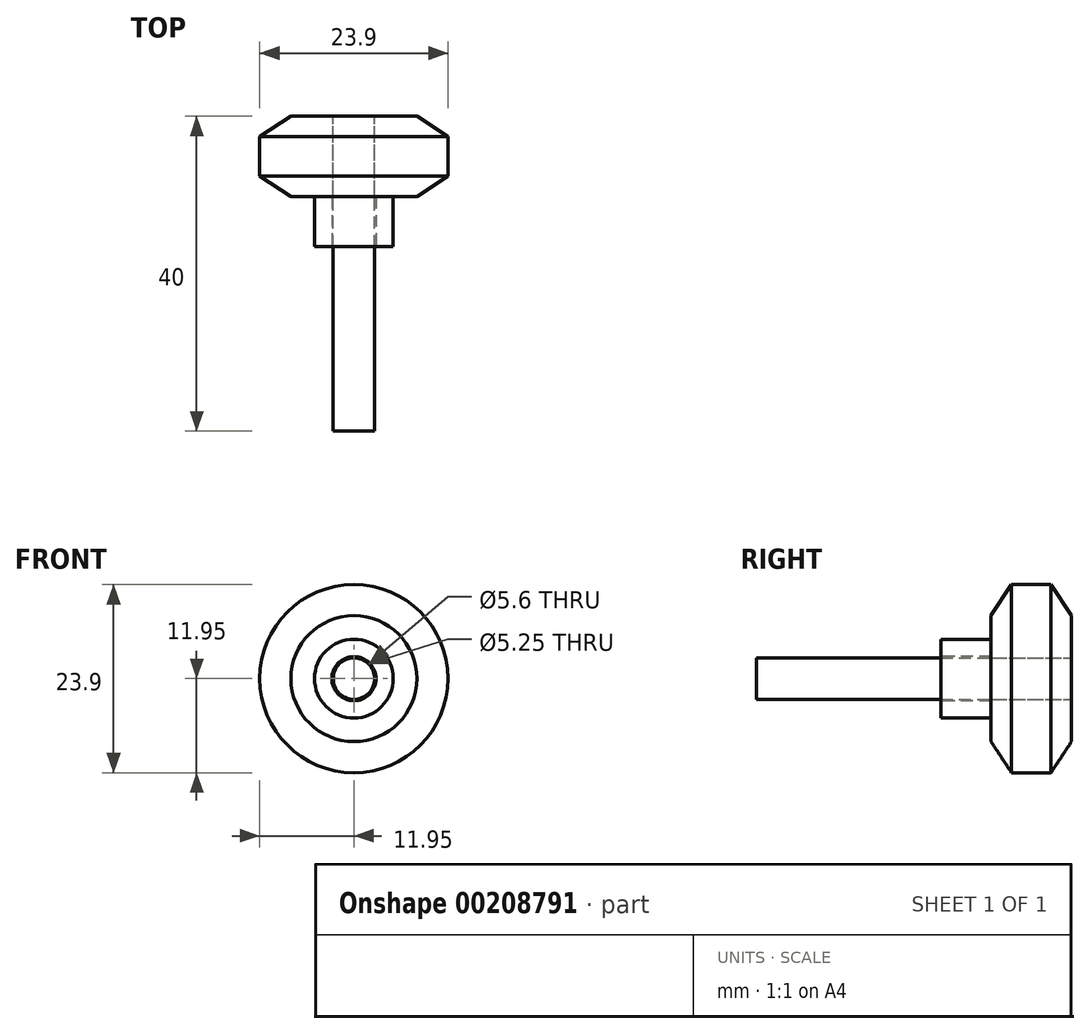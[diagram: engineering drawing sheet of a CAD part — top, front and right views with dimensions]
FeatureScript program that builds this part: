
annotation { "Feature Type Name" : "Feature", "Feature Type Description" : "" }
export const myFeature = defineFeature(function(context is Context, id is Id, definition is map)
    precondition{}
    {
        {
            var Q0;
            Q0=qCreatedBy(makeId("Right.planeOp"),FACE);
            var sketch = newSketch(context, id + "F0", { "sketchPlane" : qUnion([Q0])});
            skLineSegment(sketch, "E0", {"start": v(-2.62, 11.95) * mm, "end": v(-7.62, 11.95) * mm});
            skLineSegment(sketch, "E1", {"start": v(-7.62, 11.95) * mm, "end": v(-10.23, 8) * mm});
            skLineSegment(sketch, "E2", {"start": v(-10.23, 8) * mm, "end": v(-10.23, 0) * mm});
            skLineSegment(sketch, "E3", {"start": v(0, 0) * mm, "end": v(0, 8) * mm});
            skLineSegment(sketch, "E4", {"start": v(0, 8) * mm, "end": v(-2.62, 11.95) * mm});
            skLineSegment(sketch, "E5", {"start": v(-10.23, 0) * mm, "end": v(0, 0) * mm});
            skSolve(sketch);
        }
        {
            var Q0;
            Q0=makeQuery(id+"F0.imprint","IMPRINT",FACE,{"disambiguationData":[TD([[makeQuery(id+"F0.imprint","IMPRINT",EDGE,{"derivedFrom":sQuery(id+"F0.wireOp",EDGE,"E0")}),1.0]])]});
            var Q1;
            Q1=sQuery(id+"F0.wireOp",EDGE,"E5");
            revolve(context, id + "F1", {"entities" : qUnion([Q0]), "axis" : qUnion([Q1]), "revolveType" : RevolveType.FULL});
        }
        {
            var Q0;
            Q0=makeQuery(id+"F1.opRevolve","SWEPT_FACE",FACE,{"disambiguationData":[OSD([sQuery(id+"F0.wireOp",EDGE,"E2")])]});
            var sketch = newSketch(context, id + "F2", { "sketchPlane" : qUnion([Q0])});
            skPoint(sketch, "E6", {"position": v(0, 0) * mm});
            skSolve(sketch);
        }
        {
            var Q0;
            Q0=sQuery(id+"F2.wireOp",VERTEX,"E6");
            var Q1;
            Q1=makeQuery(id+"F1.opRevolve","SWEPT_BODY",BODY,{"disambiguationData":[OSD([sQuery(id+"F0.wireOp",EDGE,"E0"),sQuery(id+"F0.wireOp",EDGE,"E1"),sQuery(id+"F0.wireOp",EDGE,"E2"),sQuery(id+"F0.wireOp",EDGE,"E3"),sQuery(id+"F0.wireOp",EDGE,"E4"),sQuery(id+"F0.wireOp",EDGE,"E5")])]});
            hole(context, id + "F3", {"style" : HoleStyle.SIMPLE, "endStyle" : HoleEndStyle.THROUGH, "standardTappedOrClearance" : lookupTablePath({ "standard" : "ISO", "fit" : "Close", "size" : "M5", "type" : "Clearance" }), "standardBlindInLast" : lookupTablePath({ "fit" : "Close", "standard" : "ISO", "size" : "M5", "type" : "Clearance" }), "holeDiameter" : 5.25 * mm, "locations" : qUnion([Q0]), "scope" : qUnion([Q1]), "isTappedThrough" : true});
        }
        {
            var Q0;
            Q0=qCreatedBy(makeId("Front.planeOp"),FACE);
            var sketch = newSketch(context, id + "F4", { "sketchPlane" : qUnion([Q0])});
            skCircle(sketch, "E7", {"center": v(0, 0) * mm, "radius": 2.62 * mm});
            skSolve(sketch);
        }
        {
            var Q0;
            Q0=makeQuery(id+"F4.imprint","IMPRINT",FACE,{"disambiguationData":[TD([[makeQuery(id+"F4.imprint","IMPRINT",EDGE,{"derivedFrom":sQuery(id+"F4.wireOp",EDGE,"E7")}),1.0]])]});
            extrude(context, id + "F5", {"entities" : qUnion([Q0]), "depth" : 40 * mm});
        }
        {
            var Q0;
            Q0=makeQuery(id+"F1.opRevolve","SWEPT_FACE",FACE,{"disambiguationData":[OSD([sQuery(id+"F0.wireOp",EDGE,"E2")])]});
            var sketch = newSketch(context, id + "F6", { "sketchPlane" : qUnion([Q0])});
            skCircle(sketch, "E8", {"center": v(0, 0) * mm, "radius": 5 * mm});
            skSolve(sketch);
        }
        {
            var Q0;
            Q0=makeQuery(id+"F6.imprint","IMPRINT",FACE,{"disambiguationData":[TD([[makeQuery(id+"F6.imprint","IMPRINT",EDGE,{"derivedFrom":sQuery(id+"F6.wireOp",EDGE,"E8")}),1.0]])]});
            extrude(context, id + "F7", {"entities" : qUnion([Q0]), "depth" : 6.35 * mm});
        }
        {
            var Q0;
            Q0=sQuery(id+"F6.wireOp",VERTEX,"E8.center");
            var Q1;
            Q1=makeQuery(id+"F7.opExtrude","SWEPT_BODY",BODY,{"disambiguationData":[OSD([sQuery(id+"F3.hole-0.sketch.wireOp",EDGE,"core_line_2"),sQuery(id+"F3.hole-0.sketch.wireOp",EDGE,"core_line_3"),sQuery(id+"F6.wireOp",EDGE,"E8")])]});
            hole(context, id + "F8", {"style" : HoleStyle.SIMPLE, "endStyle" : HoleEndStyle.THROUGH, "oppositeDirection" : true, "holeDiameter" : 5.6 * mm, "startFromSketch" : true, "locations" : qUnion([Q0]), "scope" : qUnion([Q1]), "isTappedThrough" : true});
        }
    });
